# Revit family: Multi N DV6500N
name_source: partatom
category: Mechanical Equipment
revit_build: Autodesk Revit MEP 2013 (Build: 20120221_2030(x64)
units: mm (PartAtom-declared; Revit-internal decimal feet)

## types (1)
- Multi N DV6500N
    10 speed digital control and BMS and Internet control = Yes
    After Heater = option
    Air Filters = M5 and F20
    Anti frost protection = option
    BREEAM applicable = Yes
    Balanced supply and extract air ventilation with heat recovery = Yes
    Carbon dioxide control (optional) = Yes
    Control Optional = Humidity
    Control Optional . = Co2
    Control Optional .. = Temperature
    Control Standard = BMS/Internet
    Depth mm = 2500 mm  [stored 8.2021 ft]
    Double skinned insulated casing avoids thermal bridging = Yes
    EC motor for fine speed control and low SFP = Yes
    Electronic control panel with LCD display = Yes
    Filter maintenance reminder = Yes
    Flow = 0.0 L/s
    Frequency = 50Hz
    Heat Exchanger = Cross Counterflow
    Heat Recovery = <95%
    Height mm = 1170 mm  [stored 3.83858 ft]
    Humidity control (optional) = Yes
    Insulated Base Frame = Yes
    Interchangeable spigot connections = Yes
    Lockable doors = Yes
    Max Air Volume  m3/hr = 7200
    Meets Building regulations Pat L2A and L2B = Yes
    Model = MULTI-N DV6500N
    Part number = 9041520
    Pre Heater = option
    Roof Top model = Yes
    Safety cut off switch Pressure sensors for filter monitoring = Yes
    Summer By-pass = Automatic 100%
    Summer/Winter by-pass = Yes
    Versatile positioning ,floor and ceiling susupended options = Yes
    Voltage Supply      Single Phase = 400v ac
    Warranty = 1 Year
    Width mm = 2560 mm  [stored 8.39895 ft]

note: [stored X ft] marks values corroborated as IEEE doubles in the binary element streams (Revit-internal decimal feet)

## geometry (parser evidence)
native form markers: Sweep x1
no freeform markers — native parametric forms only
